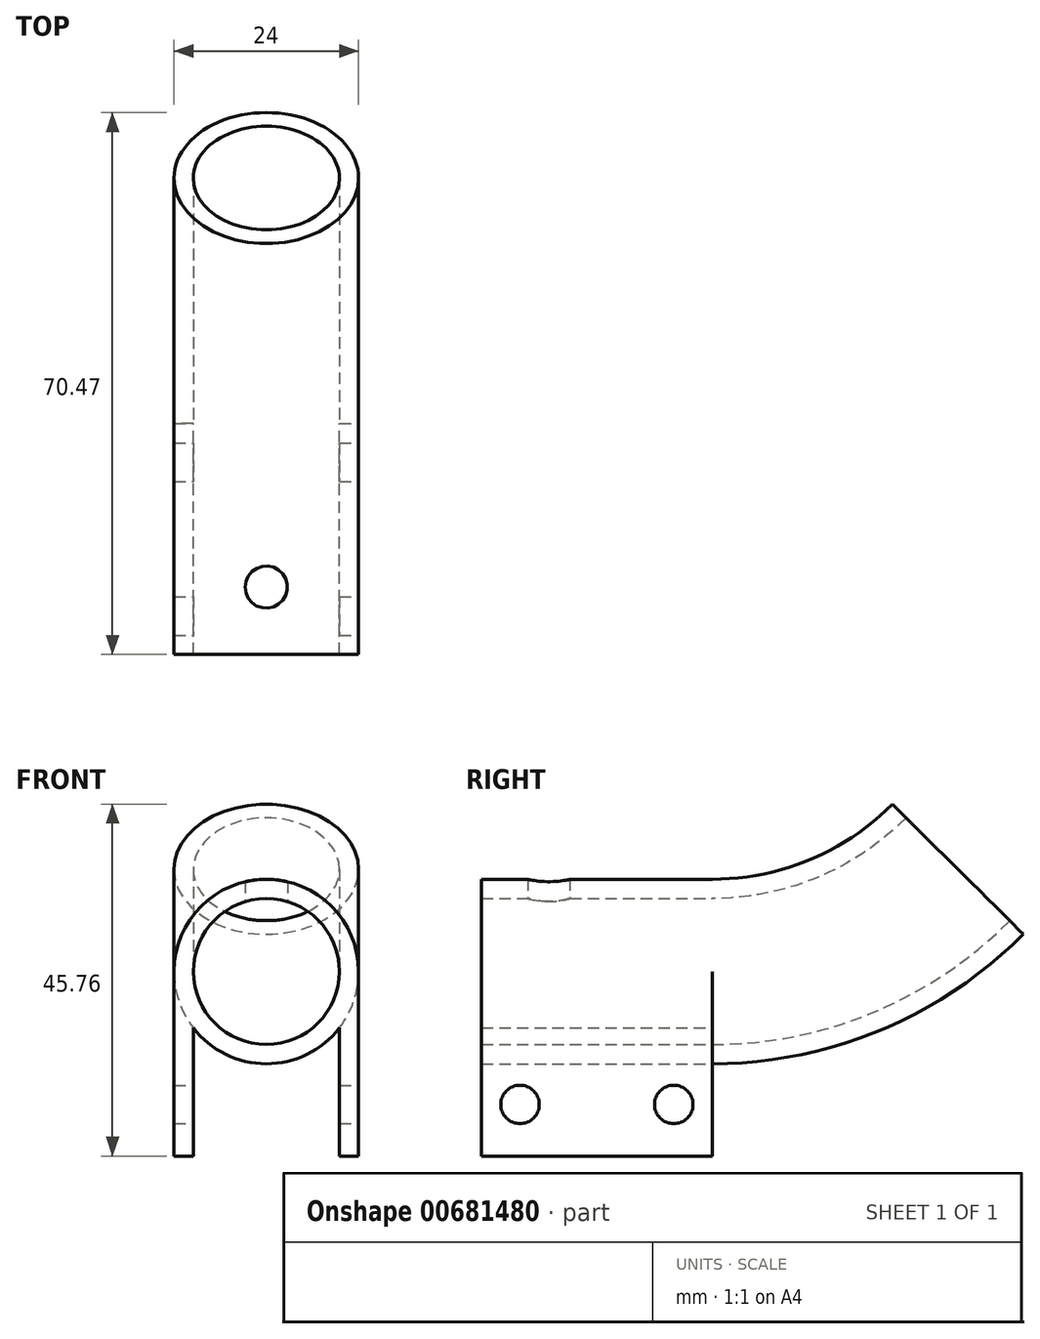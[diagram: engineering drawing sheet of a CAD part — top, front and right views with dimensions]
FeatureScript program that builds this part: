
annotation { "Feature Type Name" : "Feature", "Feature Type Description" : "" }
export const myFeature = defineFeature(function(context is Context, id is Id, definition is map)
    precondition{}
    {
        {
            var Q0;
            Q0=qCreatedBy(makeId("Front.planeOp"),FACE);
            var sketch = newSketch(context, id + "F0", { "sketchPlane" : qUnion([Q0])});
            skCircle(sketch, "E0", {"center": v(0, 0) * mm, "radius": 12 * mm});
            skCircle(sketch, "E1", {"center": v(0, 0) * mm, "radius": 9.5 * mm});
            skLineSegment(sketch, "E2.bottom", {"start": v(-9.5, 0) * mm, "end": v(-12, 0) * mm});
            skLineSegment(sketch, "E2.top", {"start": v(-9.5, -24) * mm, "end": v(-12, -24) * mm});
            skLineSegment(sketch, "E2.left", {"start": v(-9.5, 0) * mm, "end": v(-9.5, -24) * mm});
            skLineSegment(sketch, "E2.right", {"start": v(-12, 0) * mm, "end": v(-12, -24) * mm});
            skLineSegment(sketch, "E3.bottom", {"start": v(9.5, 0) * mm, "end": v(12, 0) * mm});
            skLineSegment(sketch, "E3.top", {"start": v(9.5, -24) * mm, "end": v(12, -24) * mm});
            skLineSegment(sketch, "E3.left", {"start": v(9.5, 0) * mm, "end": v(9.5, -24) * mm});
            skLineSegment(sketch, "E3.right", {"start": v(12, 0) * mm, "end": v(12, -24) * mm});
            skSolve(sketch);
        }
        {
            var Q0;
            Q0 = qSketchRegion(id + "F0", true);
            extrude(context, id + "F1", {"entities" : qUnion([Q0]), "depth" : 30 * mm, "offsetDistance" : 25 * mm});
        }
        {
            var Q0;
            Q0=qCreatedBy(makeId("Right.planeOp"),FACE);
            var sketch = newSketch(context, id + "F2", { "sketchPlane" : qUnion([Q0])});
            skArc(sketch, "E4", {"start": v(0, 0) * mm, "mid": v(17.3, 3.46) * mm, "end": v(31.95, 13.3) * mm});
            skSolve(sketch);
        }
        {
            var Q0;
            {var subQ0=sQuery(id+"F0.wireOp",EDGE,"E2.bottom");Q0=makeQuery(id+"F0.imprint","IMPRINT",FACE,{"disambiguationData":[TD([[makeQuery(id+"F0.imprint","IMPRINT",EDGE,{"derivedFrom":subQ0}),-1.0]])]});}
            var Q1;
            {var subQ0=sQuery(id+"F0.wireOp",EDGE,"E3.bottom");Q1=makeQuery(id+"F0.imprint","IMPRINT",FACE,{"disambiguationData":[TD([[makeQuery(id+"F0.imprint","IMPRINT",EDGE,{"derivedFrom":subQ0}),-1.0]])]});}
            var Q2;
            {var subQ0=sQuery(id+"F0.wireOp",EDGE,"E2.left");var subQ1=sQuery(id+"F0.wireOp",EDGE,"E0");var subQ2=makeQuery(id+"F0.imprint","INTERSECT",VERTEX,{"derivedFrom":[subQ1,subQ0]});Q2=makeQuery(id+"F0.imprint","IMPRINT",FACE,{"disambiguationData":[TD([[makeQuery(id+"F0.imprint","IMPRINT",EDGE,{"disambiguationData":[TD([[subQ2,-1.0]])],"derivedFrom":subQ1}),1.0]])]});}
            var Q3;
            {var subQ0=sQuery(id+"F0.wireOp",EDGE,"E2.bottom");Q3=makeQuery(id+"F0.imprint","IMPRINT",FACE,{"disambiguationData":[TD([[makeQuery(id+"F0.imprint","IMPRINT",EDGE,{"derivedFrom":subQ0}),1.0]])]});}
            var Q4;
            Q4=sQuery(id+"F2.wireOp",EDGE,"E4");
            sweep(context, id + "F3", {"operationType" : NewBodyOperationType.ADD, "profiles" : qUnion([Q0, Q1, Q2, Q3]), "path" : qUnion([Q4])});
        }
        {
            var Q0;
            Q0=makeQuery(id+"F1.opExtrude","SWEPT_FACE",FACE,{"disambiguationData":[OSD([sQuery(id+"F0.wireOp",EDGE,"E3.right")])]});
            var sketch = newSketch(context, id + "F4", { "sketchPlane" : qUnion([Q0])});
            skCircle(sketch, "E5", {"center": v(-5, -17.29) * mm, "radius": 2.5 * mm});
            skCircle(sketch, "E6", {"center": v(-25, -17.29) * mm, "radius": 2.5 * mm});
            skSolve(sketch);
        }
        {
            var Q0;
            Q0=makeQuery(id+"F4.imprint","IMPRINT",FACE,{"disambiguationData":[TD([[makeQuery(id+"F4.imprint","IMPRINT",EDGE,{"derivedFrom":sQuery(id+"F4.wireOp",EDGE,"E6")}),1.0]])]});
            var Q1;
            Q1=makeQuery(id+"F4.imprint","IMPRINT",FACE,{"disambiguationData":[TD([[makeQuery(id+"F4.imprint","IMPRINT",EDGE,{"derivedFrom":sQuery(id+"F4.wireOp",EDGE,"E5")}),1.0]])]});
            extrude(context, id + "F5", {"entities" : qUnion([Q0, Q1]), "operationType" : NewBodyOperationType.REMOVE, "oppositeDirection" : true, "depth" : 50 * mm, "offsetDistance" : 25 * mm});
        }
        {
            var Q0;
            Q0=qCreatedBy(makeId("Top.planeOp"),FACE);
            var sketch = newSketch(context, id + "F6", { "sketchPlane" : qUnion([Q0])});
            skCircle(sketch, "E7", {"center": v(0, -21.25) * mm, "radius": 2.75 * mm});
            skSolve(sketch);
        }
        {
            var Q0;
            Q0 = qSketchRegion(id + "F6", true);
            extrude(context, id + "F7", {"entities" : qUnion([Q0]), "operationType" : NewBodyOperationType.REMOVE, "depth" : 25 * mm, "offsetDistance" : 25 * mm});
        }
    });
